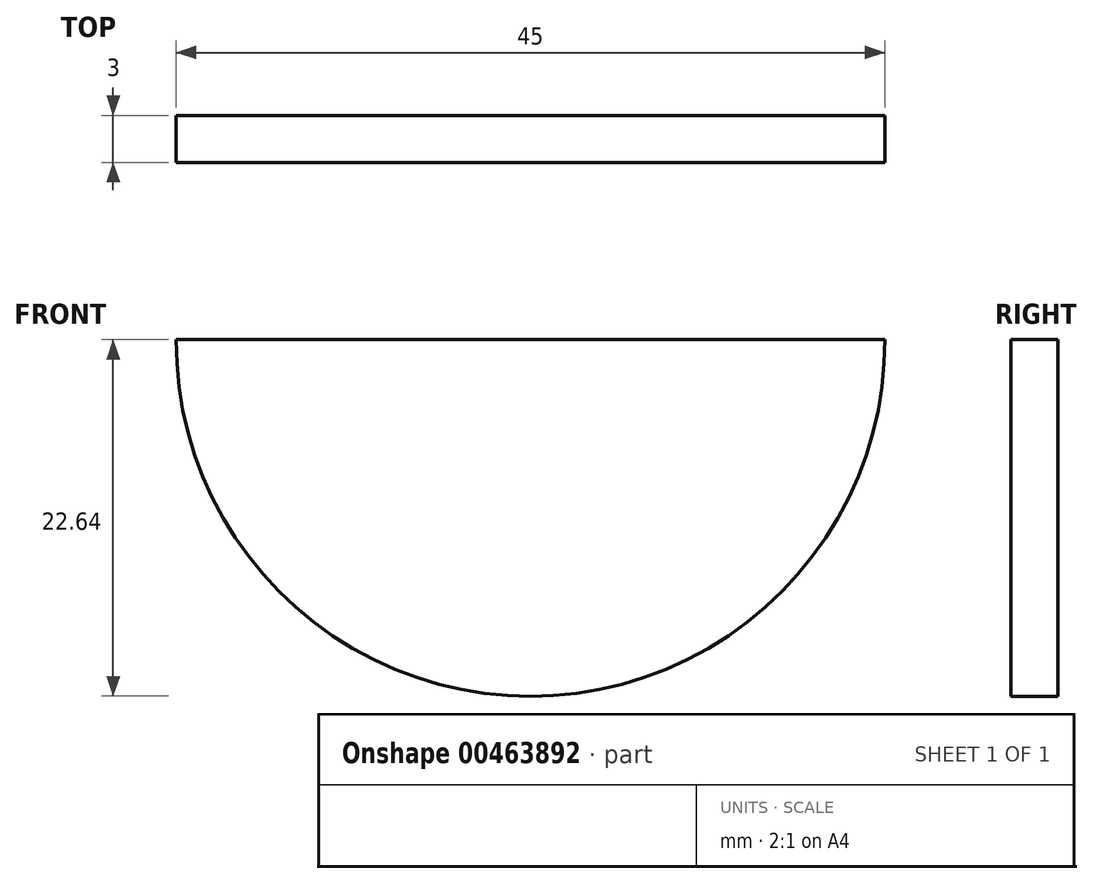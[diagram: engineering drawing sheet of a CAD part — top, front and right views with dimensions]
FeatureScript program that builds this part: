
annotation { "Feature Type Name" : "Feature", "Feature Type Description" : "" }
export const myFeature = defineFeature(function(context is Context, id is Id, definition is map)
    precondition{}
    {
        {
            var Q0;
            Q0=qCreatedBy(makeId("Front.planeOp"),FACE);
            var sketch = newSketch(context, id + "F0", { "sketchPlane" : qUnion([Q0])});
            skLineSegment(sketch, "E0", {"start": v(0, 0) * mm, "end": v(45, 0) * mm});
            skArc(sketch, "E1", {"start": v(0, 0) * mm, "mid": v(22.5, -22.64) * mm, "end": v(45, 0) * mm});
            skSolve(sketch);
        }
        {
            var Q0;
            Q0 = qSketchRegion(id + "F0", true);
            extrude(context, id + "F1", {"entities" : qUnion([Q0]), "depth" : 3 * mm});
        }
    });
